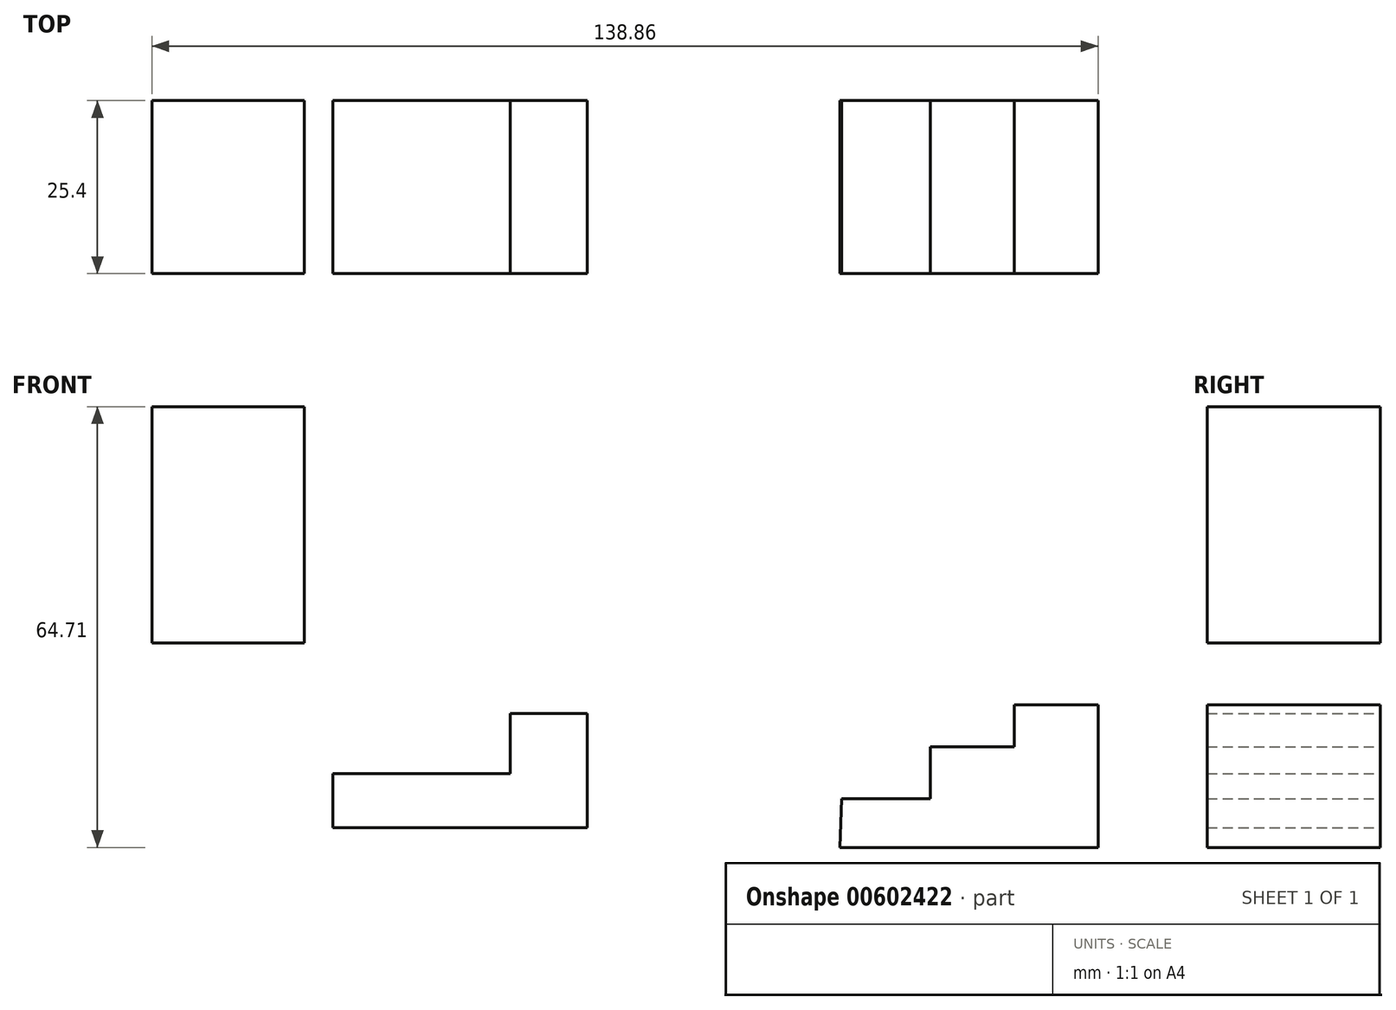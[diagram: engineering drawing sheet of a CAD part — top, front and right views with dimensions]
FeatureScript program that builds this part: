
annotation { "Feature Type Name" : "Feature", "Feature Type Description" : "" }
export const myFeature = defineFeature(function(context is Context, id is Id, definition is map)
    precondition{}
    {
        {
            var Q0;
            Q0=qCreatedBy(makeId("Front.planeOp"),FACE);
            var sketch = newSketch(context, id + "F0", { "sketchPlane" : qUnion([Q0])});
            skLineSegment(sketch, "E0", {"start": v(0, 0) * mm, "end": v(-11.33, 0) * mm});
            skLineSegment(sketch, "E1", {"start": v(-11.33, 0) * mm, "end": v(-11.33, 8.81) * mm});
            skLineSegment(sketch, "E2", {"start": v(-11.33, 8.81) * mm, "end": v(0, 8.81) * mm});
            skLineSegment(sketch, "E3", {"start": v(0, 8.81) * mm, "end": v(0, 0) * mm});
            skLineSegment(sketch, "E4", {"start": v(0, -7.97) * mm, "end": v(-11.33, -7.97) * mm});
            skLineSegment(sketch, "E5", {"start": v(-11.33, -7.97) * mm, "end": v(-11.33, 0) * mm});
            skLineSegment(sketch, "E6", {"start": v(-23.64, 0) * mm, "end": v(-23.64, -7.97) * mm});
            skLineSegment(sketch, "E7", {"start": v(-23.64, -7.97) * mm, "end": v(-11.33, -7.97) * mm});
            skLineSegment(sketch, "E8", {"start": v(-11.33, 0) * mm, "end": v(-23.64, 0) * mm});
            skLineSegment(sketch, "E9", {"start": v(0, -7.97) * mm, "end": v(0, 0) * mm});
            skLineSegment(sketch, "E10", {"start": v(-23.64, -7.97) * mm, "end": v(-37.35, -7.97) * mm});
            skLineSegment(sketch, "E11", {"start": v(-37.35, -7.97) * mm, "end": v(-37.35, 0) * mm});
            skLineSegment(sketch, "E12", {"start": v(-37.35, 0) * mm, "end": v(-23.64, 0) * mm});
            skSolve(sketch);
        }
        {
            var Q0;
            Q0 = qSketchRegion(id + "F0", true);
            extrude(context, id + "F1", {"entities" : qUnion([Q0]), "depth" : 25.4 * mm, "offsetDistance" : 25.4 * mm});
        }
        {
            var Q0;
            Q0=qCreatedBy(makeId("Front.planeOp"),FACE);
            var sketch = newSketch(context, id + "F2", { "sketchPlane" : qUnion([Q0])});
            skLineSegment(sketch, "E13", {"start": v(37.28, -3.72) * mm, "end": v(50.32, -3.72) * mm});
            skLineSegment(sketch, "E14", {"start": v(50.32, -3.72) * mm, "end": v(50.32, 3.91) * mm});
            skLineSegment(sketch, "E15", {"start": v(50.32, 3.91) * mm, "end": v(62.63, 3.91) * mm});
            skLineSegment(sketch, "E16", {"start": v(62.63, 3.91) * mm, "end": v(62.63, 10.06) * mm});
            skLineSegment(sketch, "E17", {"start": v(62.63, 10.06) * mm, "end": v(74.94, 10.06) * mm});
            skLineSegment(sketch, "E18", {"start": v(74.94, 10.06) * mm, "end": v(74.94, -3.72) * mm});
            skLineSegment(sketch, "E19", {"start": v(74.94, -3.72) * mm, "end": v(74.94, -10.86) * mm});
            skLineSegment(sketch, "E20", {"start": v(74.94, -10.86) * mm, "end": v(37.03, -10.86) * mm});
            skLineSegment(sketch, "E21", {"start": v(37.03, -10.86) * mm, "end": v(37.28, -3.72) * mm});
            skSolve(sketch);
        }
        {
            var Q0;
            Q0 = qSketchRegion(id + "F2", true);
            extrude(context, id + "F3", {"entities" : qUnion([Q0]), "depth" : 25.4 * mm, "offsetDistance" : 25.4 * mm});
        }
        {
            var Q0;
            Q0=qCreatedBy(makeId("Front.planeOp"),FACE);
            var sketch = newSketch(context, id + "F4", { "sketchPlane" : qUnion([Q0])});
            skLineSegment(sketch, "E22", {"start": v(-63.92, 31.2) * mm, "end": v(-63.92, 19.16) * mm});
            skLineSegment(sketch, "E23", {"start": v(-63.92, 19.16) * mm, "end": v(-53.01, 19.16) * mm});
            skLineSegment(sketch, "E24", {"start": v(-53.01, 19.16) * mm, "end": v(-53.01, 31.2) * mm});
            skLineSegment(sketch, "E25", {"start": v(-53.01, 31.2) * mm, "end": v(-63.92, 31.2) * mm});
            skLineSegment(sketch, "E26", {"start": v(-53.01, 19.16) * mm, "end": v(-41.54, 19.16) * mm});
            skLineSegment(sketch, "E27", {"start": v(-53.01, 31.2) * mm, "end": v(-41.54, 31.2) * mm});
            skLineSegment(sketch, "E28", {"start": v(-41.54, 31.2) * mm, "end": v(-41.54, 19.16) * mm});
            skLineSegment(sketch, "E29", {"start": v(-63.92, 31.2) * mm, "end": v(-63.92, 43.5) * mm});
            skLineSegment(sketch, "E30", {"start": v(-63.92, 43.5) * mm, "end": v(-53.01, 43.5) * mm});
            skLineSegment(sketch, "E31", {"start": v(-53.01, 43.5) * mm, "end": v(-41.54, 43.5) * mm});
            skLineSegment(sketch, "E32", {"start": v(-41.54, 43.5) * mm, "end": v(-41.54, 31.2) * mm});
            skLineSegment(sketch, "E33", {"start": v(-53.01, 31.2) * mm, "end": v(-53.01, 43.5) * mm});
            skLineSegment(sketch, "E34", {"start": v(-63.92, 43.5) * mm, "end": v(-63.92, 53.85) * mm});
            skLineSegment(sketch, "E35", {"start": v(-63.92, 53.85) * mm, "end": v(-53.01, 53.85) * mm});
            skLineSegment(sketch, "E36", {"start": v(-53.01, 53.85) * mm, "end": v(-53.01, 43.5) * mm});
            skLineSegment(sketch, "E37", {"start": v(-53.01, 53.85) * mm, "end": v(-41.54, 53.85) * mm});
            skLineSegment(sketch, "E38", {"start": v(-41.54, 53.85) * mm, "end": v(-41.54, 43.5) * mm});
            skSolve(sketch);
        }
        {
            var Q0;
            Q0 = qSketchRegion(id + "F4", true);
            extrude(context, id + "F5", {"entities" : qUnion([Q0]), "depth" : 25.4 * mm, "offsetDistance" : 25.4 * mm});
        }
        {
            var Q0;
            Q0=makeQuery(id+"F1.opExtrude","CAP_FACE",FACE,{"disambiguationData":[OSD([sQuery(id+"F0.wireOp",EDGE,"E1"),sQuery(id+"F0.wireOp",EDGE,"E2"),sQuery(id+"F0.wireOp",EDGE,"E3"),sQuery(id+"F0.wireOp",EDGE,"E4"),sQuery(id+"F0.wireOp",EDGE,"E7"),sQuery(id+"F0.wireOp",EDGE,"E8"),sQuery(id+"F0.wireOp",EDGE,"E9"),sQuery(id+"F0.wireOp",EDGE,"E10"),sQuery(id+"F0.wireOp",EDGE,"E11"),sQuery(id+"F0.wireOp",EDGE,"E12")])],"isStart":false});
            extrude(context, id + "F6", {"entities" : qUnion([Q0]), "operationType" : NewBodyOperationType.ADD, "depth" : -25.4 * mm, "offsetDistance" : 25.4 * mm});
        }
    });
